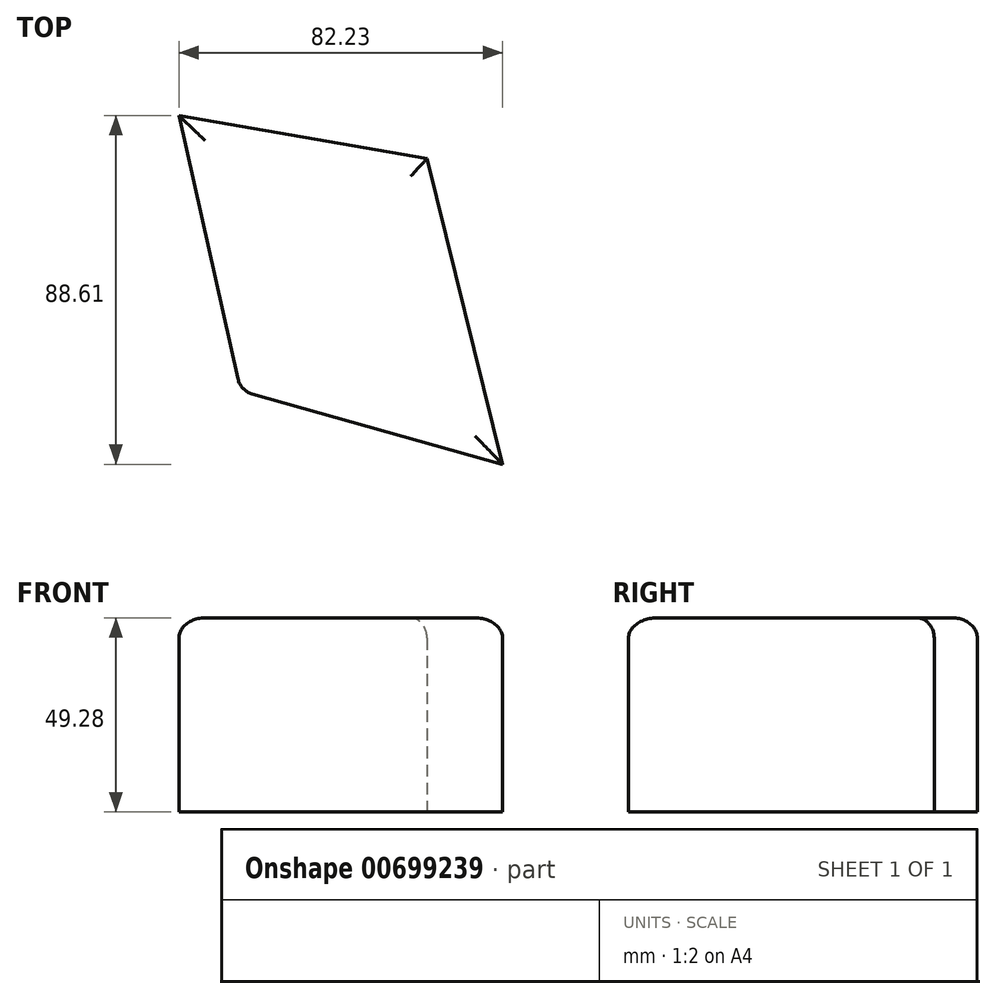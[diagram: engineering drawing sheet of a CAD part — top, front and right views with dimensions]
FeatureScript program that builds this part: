
annotation { "Feature Type Name" : "Feature", "Feature Type Description" : "" }
export const myFeature = defineFeature(function(context is Context, id is Id, definition is map)
    precondition{}
    {
        {
            var Q0;
            Q0=qCreatedBy(makeId("Top.planeOp"),FACE);
            var sketch = newSketch(context, id + "F0", { "sketchPlane" : qUnion([Q0])});
            skLineSegment(sketch, "E0", {"start": v(-109.63, 36.8) * mm, "end": v(-93.96, -33.04) * mm});
            skLineSegment(sketch, "E1", {"start": v(-93.96, -33.04) * mm, "end": v(-27.4, -51.81) * mm});
            skLineSegment(sketch, "E2", {"start": v(-27.4, -51.81) * mm, "end": v(-46.6, 25.85) * mm});
            skLineSegment(sketch, "E3", {"start": v(-46.6, 25.85) * mm, "end": v(-109.63, 36.8) * mm});
            skSolve(sketch);
        }
        {
            var Q0;
            Q0=makeQuery(id+"F0.imprint","IMPRINT",FACE,{"disambiguationData":[TD([[makeQuery(id+"F0.imprint","IMPRINT",EDGE,{"derivedFrom":sQuery(id+"F0.wireOp",EDGE,"E0")}),1.0]])]});
            extrude(context, id + "F1", {"entities" : qUnion([Q0]), "depth" : 49.28 * mm, "offsetDistance" : 25.4 * mm});
        }
        {
            var Q0;
            Q0=makeQuery(id+"F1.opExtrude","CAP_EDGE",EDGE,{"disambiguationData":[OSD([sQuery(id+"F0.wireOp",EDGE,"E0")])],"isStart":false});
            var Q1;
            Q1=makeQuery(id+"F1.opExtrude","CAP_EDGE",EDGE,{"disambiguationData":[OSD([sQuery(id+"F0.wireOp",EDGE,"E2")])],"isStart":false});
            var Q2;
            Q2=makeQuery(id+"F1.opExtrude","CAP_EDGE",EDGE,{"disambiguationData":[OSD([sQuery(id+"F0.wireOp",EDGE,"E1")])],"isStart":false});
            var Q3;
            Q3=makeQuery(id+"F1.opExtrude","CAP_EDGE",EDGE,{"disambiguationData":[OSD([sQuery(id+"F0.wireOp",EDGE,"E3")])],"isStart":false});
            var Q4;
            Q4=makeQuery(id+"F1.opExtrude","SWEPT_EDGE",EDGE,{"disambiguationData":[OSD([sQuery(id+"F0.wireOp",EDGE,"E0"),sQuery(id+"F0.wireOp",EDGE,"E1")])]});
            fillet(context, id + "F2", {"entities" : qUnion([Q0, Q1, Q2, Q3, Q4]), "radius" : 5.08 * mm, "tangentPropagation" : true, "allowEdgeOverflow" : false});
        }
    });
